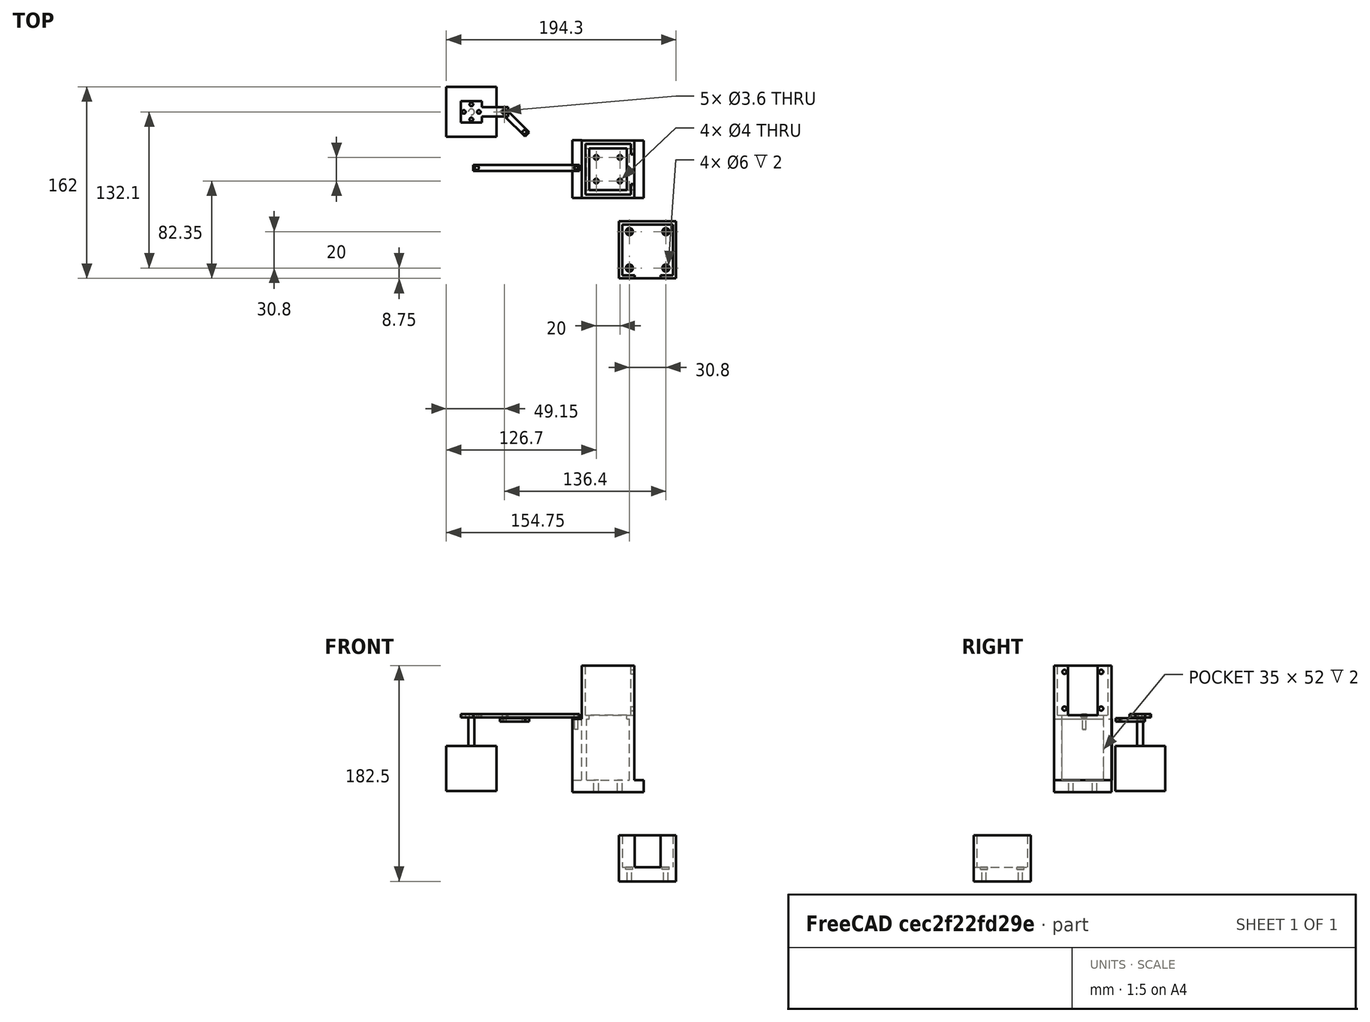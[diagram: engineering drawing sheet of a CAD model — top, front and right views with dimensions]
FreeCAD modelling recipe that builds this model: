
FCSTD DOCUMENT  (FreeCAD 0.18R16131 (Git))
Label: LinearRail
License: All rights reserved
LicenseURL: http://en.wikipedia.org/wiki/All_rights_reserved
objects: Part::Cut×32, Part::Cylinder×27, Part::Box×16, Part::MultiFuse×5
note: 80 computed .brp shape members not serialized (recipe doc carries the construction recipe); baked Part::Feature solids carry a one-line shape summary decoded from their .brp

FEATURE [Part::Box] Box  label="TrayNegative"
  AttacherType = Attacher::AttachEngine3D
  Height = 42
  Length = 38.4
  Width = 42.7
FEATURE [Part::Box] Box002  label="TrayRightCutout"
  AttacherType = Attacher::AttachEngine3D
  Height = 42
  Length = 3
  Placement = pos=(38.4,8.85,0) rot=(0,0,1;0rad)
  Width = 25
FEATURE [Part::Box] Box001  label="Tray"
  AttacherType = Attacher::AttachEngine3D
  Height = 45
  Length = 44.4
  Placement = pos=(-3,-3,-3) rot=(0,0,1;0rad)
  Width = 48.7
FEATURE [Part::Cut] Cut  label="MainTray"
  Base = -> Box001
  Tool = -> Box
FEATURE [Part::Cut] Cut001  label="CircularMotorTray"
  Base = -> Cut
  Placement = pos=(0,0,5) rot=(0,0,1;0rad)
  Tool = -> Box002
FEATURE [Part::Cylinder] Cylinder
  Angle = 360
  AttacherType = Attacher::AttachEngine3D
  Height = 10
  Placement = pos=(31.4,5.85,10.65) rot=(0,1,0;1.5708rad)
  Radius = 1.8
FEATURE [Part::Cylinder] Cylinder001
  Angle = 360
  AttacherType = Attacher::AttachEngine3D
  Height = 10
  Placement = pos=(31.4,36.85,10.65) rot=(0,1,0;1.5708rad)
  Radius = 1.8
FEATURE [Part::Cylinder] Cylinder002
  Angle = 360
  AttacherType = Attacher::AttachEngine3D
  Height = 10
  Placement = pos=(31.4,5.85,41.65) rot=(0,1,0;1.5708rad)
  Radius = 1.8
FEATURE [Part::Cylinder] Cylinder003
  Angle = 360
  AttacherType = Attacher::AttachEngine3D
  Height = 10
  Placement = pos=(31.4,36.85,41.65) rot=(0,1,0;1.5708rad)
  Radius = 1.8
FEATURE [Part::Cut] Cut002
  Base = -> Cut001
  Tool = -> Cylinder
FEATURE [Part::Cut] Cut003
  Base = -> Cut002
  Tool = -> Cylinder001
FEATURE [Part::Cut] Cut004
  Base = -> Cut003
  Tool = -> Cylinder002
FEATURE [Part::Cut] Cut005
  Base = -> Cut004
  Tool = -> Cylinder003
FEATURE [Part::Box] Box003  label="Cube"
  AttacherType = Attacher::AttachEngine3D
  Height = 10
  Length = 60
  Placement = pos=(-4.6,-3,-32) rot=(0,0,1;0rad)
  Width = 48.7
FEATURE [Part::Cylinder] Cylinder004
  Angle = 360
  AttacherType = Attacher::AttachEngine3D
  Height = 15
  Placement = pos=(15.4,11.35,-35) rot=(0,0,1;0rad)
  Radius = 2
FEATURE [Part::Cylinder] Cylinder005
  Angle = 360
  AttacherType = Attacher::AttachEngine3D
  Height = 15
  Placement = pos=(35.4,11.35,-35) rot=(0,0,1;0rad)
  Radius = 2
FEATURE [Part::Cylinder] Cylinder006
  Angle = 360
  AttacherType = Attacher::AttachEngine3D
  Height = 15
  Placement = pos=(15.4,31.35,-35) rot=(0,0,1;0rad)
  Radius = 2
FEATURE [Part::Cylinder] Cylinder007
  Angle = 360
  AttacherType = Attacher::AttachEngine3D
  Height = 15
  Placement = pos=(35.4,31.35,-35) rot=(0,0,1;0rad)
  Radius = 2
FEATURE [Part::Cut] Cut006
  Base = -> Box003
  Tool = -> Cylinder004
FEATURE [Part::Cut] Cut007
  Base = -> Cut006
  Tool = -> Cylinder005
FEATURE [Part::Cut] Cut008
  Base = -> Cut007
  Tool = -> Cylinder006
FEATURE [Part::Cut] Cut009
  Base = -> Cut008
  Tool = -> Cylinder007
FEATURE [Part::Box] Box004  label="Cube001"
  AttacherType = Attacher::AttachEngine3D
  Height = 10
  Length = 32
  Placement = pos=(3.2,3.85,0) rot=(0,0,1;0rad)
  Width = 35
FEATURE [Part::Cut] Cut010
  Base = -> Cut005
  Placement = pos=(6.2,0,28) rot=(0,0,1;0rad)
  Tool = -> Box004
FEATURE [Part::Box] Box005  label="Tray001"
  AttacherType = Attacher::AttachEngine3D
  Height = 52
  Length = 44.4
  Placement = pos=(3.2,-3,-22) rot=(0,0,1;0rad)
  Width = 48.7
FEATURE [Part::Box] Box006  label="Cube002"
  AttacherType = Attacher::AttachEngine3D
  Height = 52
  Length = 36
  Placement = pos=(7.4,3.85,-22) rot=(0,0,1;0rad)
  Width = 35
FEATURE [Part::Cut] Cut011
  Base = -> Box005
  Tool = -> Box006
FEATURE [Part::MultiFuse] Fusion
  Shapes = -> [Cut009,Cut010,Cut011]
FEATURE [Part::Box] Box007  label="Cube003"
  AttacherType = Attacher::AttachEngine3D
  Height = 52
  Length = 7.8
  Placement = pos=(-4.6,-3,-22) rot=(0,0,1;0rad)
  Width = 48.8
FEATURE [Part::MultiFuse] Fusion001
  Shapes = -> [Box007,Fusion]
FEATURE [Part::Cylinder] Cylinder015
  Angle = 360
  AttacherType = Attacher::AttachEngine3D
  Height = 10
  Placement = pos=(27,2.5,0) rot=(0,0,1;0rad)
  Radius = 1.7
FEATURE [Part::Box] Box015  label="StaticTray"
  AttacherType = Attacher::AttachEngine3D
  Height = 48.3
  Length = 48.3
  Placement = pos=(91,0,0) rot=(0,0,1;0rad)
  Width = 39
FEATURE [Part::Box] Box016  label="StaticTrayNegative"
  AttacherType = Attacher::AttachEngine3D
  Height = 42.8
  Length = 42.8
  Placement = pos=(93.75,0,2.75) rot=(0,0,1;0rad)
  Width = 27
FEATURE [Part::Cut] Cut017  label="LinearMotorTray"
  Base = -> Box015
  Placement = pos=(-56.3,68.5,-71) rot=(0,0,1;0rad)
  Tool = -> Box016
FEATURE [Part::Box] Box019  label="Cube004"
  AttacherType = Attacher::AttachEngine3D
  Height = 10
  Length = 22
  Placement = pos=(47.85,68.5,-75) rot=(0,0,1;0rad)
  Width = 27
FEATURE [Part::Cut] Cut018  label="LinearTray"
  Base = -> Cut017
  Placement = pos=(0,0,0) rot=(-1,0,0;1.5708rad)
  Tool = -> Box019
FEATURE [Part::Box] Box014  label="SliderArm"
  AttacherType = Attacher::AttachEngine3D
  Height = 3
  Length = 30
  Width = 5
FEATURE [Part::Cylinder] Cylinder008  label="Rotor001"
  Angle = 360
  AttacherType = Attacher::AttachEngine3D
  Height = 24
  Placement = pos=(21.15,21.15,38) rot=(0,0,1;0rad)
  Radius = 2.5
FEATURE [Part::Box] Box011  label="Motor001"
  AttacherType = Attacher::AttachEngine3D
  Height = 38
  Length = 42.3
  Width = 42.3
FEATURE [Part::MultiFuse] Fusion004  label="17HS4401-2"
  Placement = pos=(69,97,-48) rot=(1,0,0;1.5708rad)
  Shapes = -> [Box011,Cylinder008]
FEATURE [Part::Box] Box012  label="SlideMotorArm"
  AttacherType = Attacher::AttachEngine3D
  Height = 3
  Length = 18
  Placement = pos=(-4,21,0) rot=(0,0,1;0rad)
  Width = 18
FEATURE [Part::Cylinder] Cylinder009
  Angle = 360
  AttacherType = Attacher::AttachEngine3D
  Height = 10
  Placement = pos=(-1.35,30,0) rot=(0,0,1;0rad)
  Radius = 1.5
FEATURE [Part::Cylinder] Cylinder011
  Angle = 360
  AttacherType = Attacher::AttachEngine3D
  Height = 10
  Placement = pos=(5,2,0) rot=(0,0,1;0rad)
  Radius = 1.8
FEATURE [Part::Cylinder] Cylinder012
  Angle = 360
  AttacherType = Attacher::AttachEngine3D
  Height = 10
  Placement = pos=(11.35,30,0) rot=(0,0,1;0rad)
  Radius = 1.5
FEATURE [Part::Cylinder] Cylinder013
  Angle = 360
  AttacherType = Attacher::AttachEngine3D
  Height = 10
  Placement = pos=(5,36.35,0) rot=(0,0,1;0rad)
  Radius = 1.5
FEATURE [Part::Cut] Cut020
  Base = -> Box012
  Tool = -> Cylinder013
FEATURE [Part::Cut] Cut012
  Base = -> Cut020
  Tool = -> Cylinder012
FEATURE [Part::Cut] Cut019
  Base = -> Cut012
  Tool = -> Cylinder009
FEATURE [Part::Cylinder] Cylinder014
  Angle = 360
  AttacherType = Attacher::AttachEngine3D
  Height = 10
  Placement = pos=(3,2.5,0) rot=(0,0,1;0rad)
  Radius = 1.7
FEATURE [Part::Cut] Cut016
  Base = -> Box014
  Tool = -> Cylinder014
FEATURE [Part::Cut] Cut015  label="SlideArm"
  Base = -> Cut016
  Placement = pos=(41.4,38.5,-9.5) rot=(0.862856,0.357407,-0.357407;1.71777rad)
  Tool = -> Cylinder015
FEATURE [Part::Cylinder] Cylinder010
  Angle = 360
  AttacherType = Attacher::AttachEngine3D
  Height = 10
  Placement = pos=(5,23.65,0) rot=(0,0,1;0rad)
  Radius = 1.5
FEATURE [Part::Cut] Cut014
  Base = -> Cut019
  Tool = -> Cylinder010
FEATURE [Part::Box] Box013  label="SlideMotorArmExt"
  AttacherType = Attacher::AttachEngine3D
  Height = 3
  Length = 8
  Placement = pos=(1,-1,0) rot=(0,0,1;0rad)
  Width = 22
FEATURE [Part::Cut] Cut013
  Base = -> Box013
  Tool = -> Cylinder011
FEATURE [Part::MultiFuse] Fusion005  label="SlideMotorArmExtension"
  Placement = pos=(60.15,35,-21.85) rot=(0.57735,0.57735,-0.57735;2.0944rad)
  Shapes = -> [Cut014,Cut013]
FEATURE [Part::MultiFuse] Fusion006  label="SlidingMotorConfig"
  Placement = pos=(0,43,66) rot=(0,0.707107,-0.707107;3.14159rad)
  Shapes = -> [Fusion004,Fusion005,Cut015]
FEATURE [Part::Box] Box020  label="SliderArm001"
  AttacherType = Attacher::AttachEngine3D
  Height = 3
  Length = 90
  Width = 5
FEATURE [Part::Cylinder] Cylinder016
  Angle = 360
  AttacherType = Attacher::AttachEngine3D
  Height = 10
  Placement = pos=(87,2.5,0) rot=(0,0,1;0rad)
  Radius = 1.7
FEATURE [Part::Cylinder] Cylinder017
  Angle = 360
  AttacherType = Attacher::AttachEngine3D
  Height = 10
  Placement = pos=(3,2.5,0) rot=(0,0,1;0rad)
  Radius = 1.7
FEATURE [Part::Cut] Cut021
  Base = -> Box020
  Tool = -> Cylinder017
FEATURE [Part::Cut] Cut022  label="SlideArm001"
  Base = -> Cut021
  Placement = pos=(-88.6,20,31) rot=(0,0,1;0rad)
  Tool = -> Cylinder016
FEATURE [Part::Cylinder] Cylinder018
  Angle = 360
  AttacherType = Attacher::AttachEngine3D
  Height = 20
  Placement = pos=(74.25,-62.25,-110) rot=(0,0,1;0rad)
  Radius = 1.8
FEATURE [Part::Cylinder] Cylinder019
  Angle = 360
  AttacherType = Attacher::AttachEngine3D
  Height = 20
  Placement = pos=(74.25,-31.45,-110) rot=(0,0,1;0rad)
  Radius = 1.8
FEATURE [Part::Cylinder] Cylinder020
  Angle = 360
  AttacherType = Attacher::AttachEngine3D
  Height = 20
  Placement = pos=(43.45,-62.25,-110) rot=(0,0,1;0rad)
  Radius = 1.8
FEATURE [Part::Cylinder] Cylinder021
  Angle = 360
  AttacherType = Attacher::AttachEngine3D
  Height = 20
  Placement = pos=(43.45,-31.45,-110) rot=(0,0,1;0rad)
  Radius = 1.8
FEATURE [Part::Cut] Cut023
  Base = -> Cut018
  Tool = -> Cylinder018
FEATURE [Part::Cut] Cut024
  Base = -> Cut023
  Tool = -> Cylinder019
FEATURE [Part::Cut] Cut025
  Base = -> Cut024
  Tool = -> Cylinder020
FEATURE [Part::Cut] Cut026
  Base = -> Cut025
  Tool = -> Cylinder021
FEATURE [Part::Cylinder] Cylinder022
  Angle = 360
  AttacherType = Attacher::AttachEngine3D
  Height = 10
  Placement = pos=(43.45,-31.45,-97.5) rot=(0,0,1;0rad)
  Radius = 3
FEATURE [Part::Cut] Cut027
  Base = -> Cut026
  Tool = -> Cylinder022
FEATURE [Part::Cylinder] Cylinder023
  Angle = 360
  AttacherType = Attacher::AttachEngine3D
  Height = 10
  Placement = pos=(74.25,-31.45,-97.5) rot=(0,0,1;0rad)
  Radius = 3
FEATURE [Part::Cut] Cut028
  Base = -> Cut027
  Tool = -> Cylinder023
FEATURE [Part::Cylinder] Cylinder024
  Angle = 360
  AttacherType = Attacher::AttachEngine3D
  Height = 10
  Placement = pos=(74.25,-62.25,-97.5) rot=(0,0,1;0rad)
  Radius = 3
FEATURE [Part::Cut] Cut029
  Base = -> Cut028
  Tool = -> Cylinder024
FEATURE [Part::Cylinder] Cylinder025
  Angle = 360
  AttacherType = Attacher::AttachEngine3D
  Height = 10
  Placement = pos=(43.45,-62.25,-97.5) rot=(0,0,1;0rad)
  Radius = 3
FEATURE [Part::Cut] Cut030
  Base = -> Cut029
  Tool = -> Cylinder025
FEATURE [Part::Cylinder] Cylinder026
  Angle = 360
  AttacherType = Attacher::AttachEngine3D
  Height = 10
  Placement = pos=(-1.5,22.5,21) rot=(0,0,1;0rad)
  Radius = 1.4
FEATURE [Part::Cut] Cut031
  Base = -> Fusion001
  Tool = -> Cylinder026
